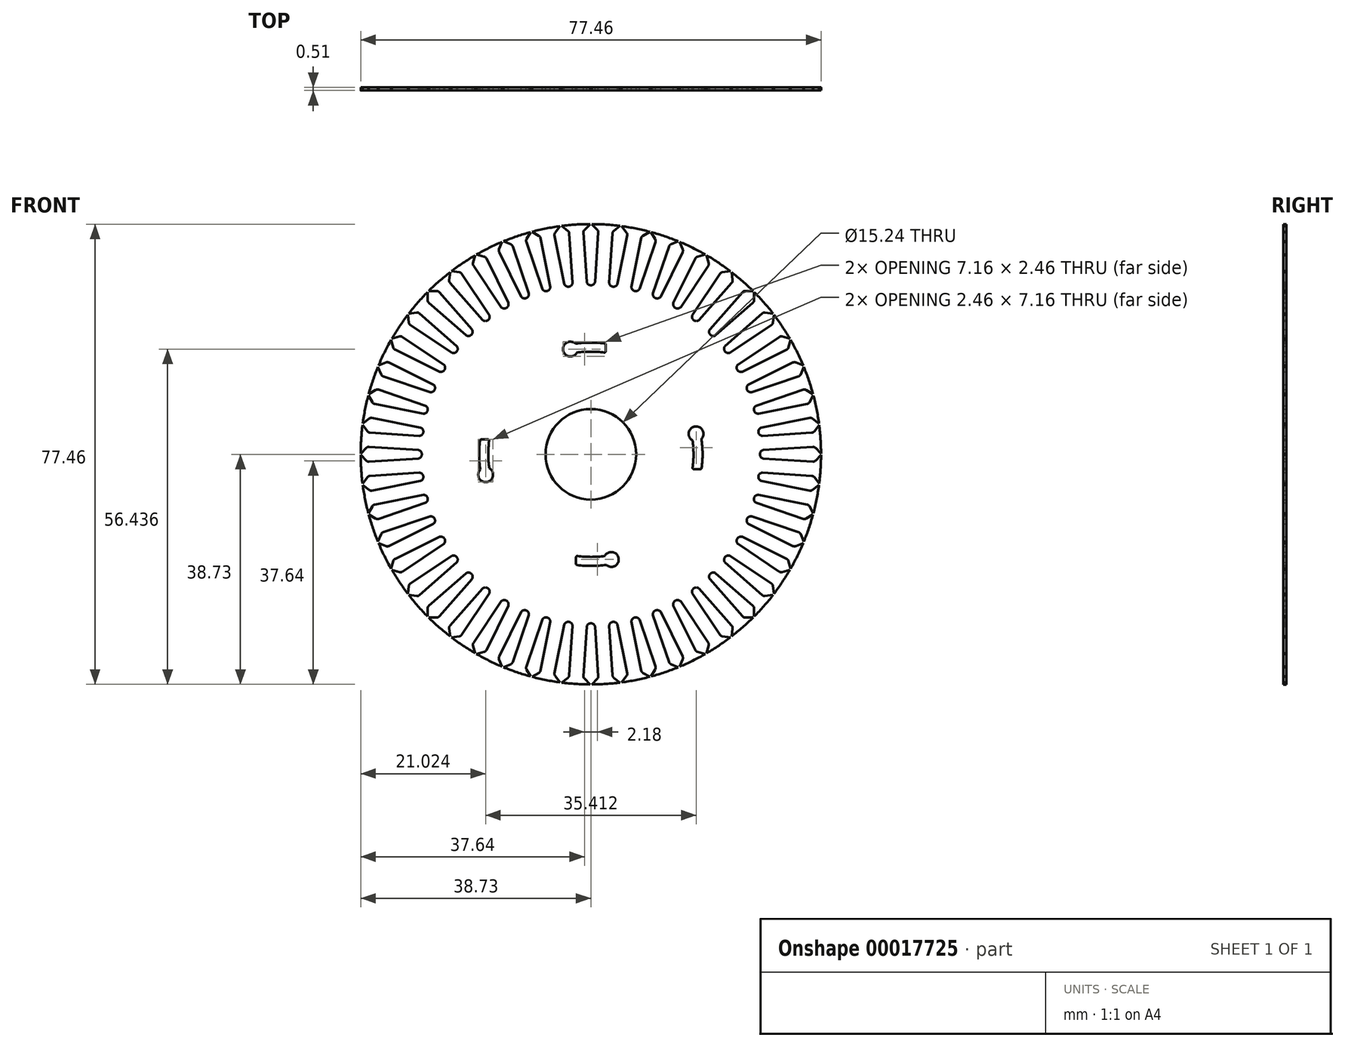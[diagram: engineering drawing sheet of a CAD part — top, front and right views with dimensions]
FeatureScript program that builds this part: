
annotation { "Feature Type Name" : "Feature", "Feature Type Description" : "" }
export const myFeature = defineFeature(function(context is Context, id is Id, definition is map)
    precondition{}
    {
        {
            var Q0;
            Q0=qCreatedBy(makeId("Front.planeOp"),FACE);
            var sketch = newSketch(context, id + "F0", { "sketchPlane" : qUnion([Q0])});
            skCircle(sketch, "E0", {"center": v(0, 0) * mm, "radius": 7.62 * mm});
            skArc(sketch, "E1", {"start": v(-0.12, 38.73) * mm, "mid": v(-2.53, 38.65) * mm, "end": v(-4.93, 38.42) * mm});
            skLineSegment(sketch, "E2", {"start": v(0, 0) * mm, "end": v(-4.84, 24.91) * mm, "construction": true});
            skArc(sketch, "E3", {"start": v(2.27, 17.12) * mm, "mid": v(-0.04, 17.27) * mm, "end": v(-2.35, 17.11) * mm});
            skArc(sketch, "E4", {"start": v(2.32, 18.65) * mm, "mid": v(-0.14, 18.8) * mm, "end": v(-2.6, 18.62) * mm});
            skArc(sketch, "E5", {"start": v(-2.6, 18.62) * mm, "mid": v(-4.67, 17.5) * mm, "end": v(-2.35, 17.11) * mm});
            skLineSegment(sketch, "E6", {"start": v(0, 17.1) * mm, "end": v(2.49, 17.1) * mm, "construction": true});
            skLineSegment(sketch, "E7", {"start": v(2.49, 17.32) * mm, "end": v(2.49, 18.46) * mm});
            skArc(sketch, "E8.1.0", {"start": v(-18.62, -2.6) * mm, "mid": v(-17.5, -4.67) * mm, "end": v(-17.11, -2.35) * mm});
            skArc(sketch, "E8.1.1", {"start": v(-18.65, 2.32) * mm, "mid": v(-18.8, -0.14) * mm, "end": v(-18.62, -2.6) * mm});
            skLineSegment(sketch, "E8.1.2", {"start": v(-17.32, 2.49) * mm, "end": v(-18.46, 2.49) * mm});
            skArc(sketch, "E8.1.3", {"start": v(-17.12, 2.27) * mm, "mid": v(-17.27, -0.04) * mm, "end": v(-17.11, -2.35) * mm});
            skArc(sketch, "E8.2.0", {"start": v(2.6, -18.62) * mm, "mid": v(4.67, -17.5) * mm, "end": v(2.35, -17.11) * mm});
            skArc(sketch, "E8.2.1", {"start": v(-2.32, -18.65) * mm, "mid": v(0.14, -18.8) * mm, "end": v(2.6, -18.62) * mm});
            skLineSegment(sketch, "E8.2.2", {"start": v(-2.49, -17.32) * mm, "end": v(-2.49, -18.46) * mm});
            skArc(sketch, "E8.2.3", {"start": v(-2.27, -17.12) * mm, "mid": v(0.04, -17.27) * mm, "end": v(2.35, -17.11) * mm});
            skArc(sketch, "E8.3.0", {"start": v(18.62, 2.6) * mm, "mid": v(17.5, 4.67) * mm, "end": v(17.11, 2.35) * mm});
            skArc(sketch, "E8.3.1", {"start": v(18.65, -2.32) * mm, "mid": v(18.8, 0.14) * mm, "end": v(18.62, 2.6) * mm});
            skLineSegment(sketch, "E8.3.2", {"start": v(17.32, -2.49) * mm, "end": v(18.46, -2.49) * mm});
            skArc(sketch, "E8.3.3", {"start": v(17.12, -2.27) * mm, "mid": v(17.27, 0.04) * mm, "end": v(17.11, 2.35) * mm});
            skPoint(sketch, "E9.visualSharp", {"position": v(2.49, 18.63) * mm});
            skArc(sketch, "E9.filletArc", {"start": v(2.49, 18.46) * mm, "mid": v(2.44, 18.59) * mm, "end": v(2.32, 18.65) * mm});
            skPoint(sketch, "E10.visualSharp", {"position": v(2.49, 17.1) * mm});
            skArc(sketch, "E10.filletArc", {"start": v(2.27, 17.12) * mm, "mid": v(2.42, 17.17) * mm, "end": v(2.49, 17.32) * mm});
            skPoint(sketch, "E11.visualSharp", {"position": v(-18.63, 2.49) * mm});
            skArc(sketch, "E11.filletArc", {"start": v(-18.46, 2.49) * mm, "mid": v(-18.59, 2.44) * mm, "end": v(-18.65, 2.32) * mm});
            skPoint(sketch, "E12.visualSharp", {"position": v(-17.1, 2.49) * mm});
            skArc(sketch, "E12.filletArc", {"start": v(-17.12, 2.27) * mm, "mid": v(-17.17, 2.42) * mm, "end": v(-17.32, 2.49) * mm});
            skPoint(sketch, "E13.visualSharp", {"position": v(-2.49, -18.63) * mm});
            skArc(sketch, "E13.filletArc", {"start": v(-2.49, -18.46) * mm, "mid": v(-2.44, -18.59) * mm, "end": v(-2.32, -18.65) * mm});
            skPoint(sketch, "E14.visualSharp", {"position": v(-2.49, -17.1) * mm});
            skArc(sketch, "E14.filletArc", {"start": v(-2.27, -17.12) * mm, "mid": v(-2.42, -17.17) * mm, "end": v(-2.49, -17.32) * mm});
            skPoint(sketch, "E15.visualSharp", {"position": v(18.63, -2.49) * mm});
            skArc(sketch, "E15.filletArc", {"start": v(18.46, -2.49) * mm, "mid": v(18.59, -2.44) * mm, "end": v(18.65, -2.32) * mm});
            skPoint(sketch, "E16.visualSharp", {"position": v(17.1, -2.49) * mm});
            skArc(sketch, "E16.filletArc", {"start": v(17.12, -2.27) * mm, "mid": v(17.17, -2.42) * mm, "end": v(17.32, -2.49) * mm});
            skLineSegment(sketch, "E17", {"start": v(0, 0) * mm, "end": v(5.53, 45) * mm, "construction": true});
            skLineSegment(sketch, "E18", {"start": v(-18.4, 38.5) * mm, "end": v(-0.35, 38.5) * mm, "construction": true});
            skPoint(sketch, "E19", {"position": v(-0.35, 38.5) * mm});
            skPoint(sketch, "E20", {"position": v(0.35, 38.5) * mm});
            skLineSegment(sketch, "E21", {"start": v(0.35, 38.5) * mm, "end": v(1.08, 37.77) * mm});
            skLineSegment(sketch, "E22", {"start": v(-0.35, 38.5) * mm, "end": v(-1.08, 37.77) * mm});
            skLineSegment(sketch, "E23", {"start": v(-0.35, 38.5) * mm, "end": v(-0.12, 38.73) * mm});
            skLineSegment(sketch, "E24", {"start": v(0.35, 38.5) * mm, "end": v(0.12, 38.73) * mm});
            skLineSegment(sketch, "E25", {"start": v(0.7, 29) * mm, "end": v(1.25, 37.34) * mm});
            skLineSegment(sketch, "E26", {"start": v(-0.7, 29) * mm, "end": v(-1.25, 37.34) * mm});
            skPoint(sketch, "E27", {"position": v(-1.32, 38.5) * mm});
            skPoint(sketch, "E28", {"position": v(1.32, 38.5) * mm});
            skPoint(sketch, "E29.newPointA", {"position": v(-1.7, 44.35) * mm});
            skArc(sketch, "E29.filletArc", {"start": v(-1.08, 37.77) * mm, "mid": v(-1.21, 37.58) * mm, "end": v(-1.25, 37.34) * mm});
            skPoint(sketch, "E30.newPointB", {"position": v(1.7, 44.35) * mm});
            skArc(sketch, "E30.filletArc", {"start": v(1.25, 37.34) * mm, "mid": v(1.21, 37.58) * mm, "end": v(1.08, 37.77) * mm});
            skLineSegment(sketch, "E31.trimOffspring", {"start": v(0.35, 38.5) * mm, "end": v(19.4, 38.5) * mm, "construction": true});
            skPoint(sketch, "E32.orphan", {"position": v(-0.67, 28.44) * mm});
            skArc(sketch, "E33.trimOffspring", {"start": v(-0.67, 28.44) * mm, "mid": v(0, -28.45) * mm, "end": v(0.67, 28.44) * mm, "construction": true});
            skArc(sketch, "E34.trimOffspring", {"start": v(-0.7, 29) * mm, "mid": v(0, 28.44) * mm, "end": v(0.7, 29) * mm});
            skLineSegment(sketch, "E35.1.0", {"start": v(-5.37, 38.13) * mm, "end": v(-5.18, 38.39) * mm});
            skLineSegment(sketch, "E35.1.1", {"start": v(-5.37, 38.13) * mm, "end": v(-6, 37.3) * mm});
            skArc(sketch, "E35.1.2", {"start": v(-6, 37.3) * mm, "mid": v(-6.1, 37.1) * mm, "end": v(-6.1, 36.86) * mm});
            skLineSegment(sketch, "E35.1.3", {"start": v(-4.48, 28.66) * mm, "end": v(-6.1, 36.86) * mm});
            skArc(sketch, "E35.1.4", {"start": v(-4.48, 28.66) * mm, "mid": v(-3.71, 28.2) * mm, "end": v(-3.09, 28.84) * mm});
            skLineSegment(sketch, "E35.1.5", {"start": v(-3.09, 28.84) * mm, "end": v(-3.64, 37.19) * mm});
            skArc(sketch, "E35.1.6", {"start": v(-3.64, 37.19) * mm, "mid": v(-3.7, 37.41) * mm, "end": v(-3.86, 37.6) * mm});
            skLineSegment(sketch, "E35.1.7", {"start": v(-4.68, 38.22) * mm, "end": v(-3.86, 37.6) * mm});
            skLineSegment(sketch, "E35.1.8", {"start": v(-4.68, 38.22) * mm, "end": v(-4.93, 38.42) * mm});
            skLineSegment(sketch, "E35.2.0", {"start": v(-10.3, 37.1) * mm, "end": v(-10.14, 37.38) * mm});
            skLineSegment(sketch, "E35.2.1", {"start": v(-10.3, 37.1) * mm, "end": v(-10.82, 36.2) * mm});
            skArc(sketch, "E35.2.2", {"start": v(-10.82, 36.2) * mm, "mid": v(-10.9, 35.98) * mm, "end": v(-10.87, 35.75) * mm});
            skLineSegment(sketch, "E35.2.3", {"start": v(-8.18, 27.83) * mm, "end": v(-10.87, 35.75) * mm});
            skArc(sketch, "E35.2.4", {"start": v(-8.18, 27.83) * mm, "mid": v(-7.36, 27.47) * mm, "end": v(-6.83, 28.2) * mm});
            skLineSegment(sketch, "E35.2.5", {"start": v(-6.83, 28.2) * mm, "end": v(-8.46, 36.4) * mm});
            skArc(sketch, "E35.2.6", {"start": v(-8.46, 36.4) * mm, "mid": v(-8.56, 36.6) * mm, "end": v(-8.73, 36.77) * mm});
            skLineSegment(sketch, "E35.2.7", {"start": v(-9.63, 37.29) * mm, "end": v(-8.73, 36.77) * mm});
            skLineSegment(sketch, "E35.2.8", {"start": v(-9.63, 37.29) * mm, "end": v(-9.9, 37.45) * mm});
            skLineSegment(sketch, "E35.3.0", {"start": v(-15.06, 35.44) * mm, "end": v(-14.94, 35.74) * mm});
            skLineSegment(sketch, "E35.3.1", {"start": v(-15.06, 35.44) * mm, "end": v(-15.46, 34.48) * mm});
            skArc(sketch, "E35.3.2", {"start": v(-15.46, 34.48) * mm, "mid": v(-15.5, 34.25) * mm, "end": v(-15.44, 34.02) * mm});
            skLineSegment(sketch, "E35.3.3", {"start": v(-11.75, 26.52) * mm, "end": v(-15.44, 34.02) * mm});
            skArc(sketch, "E35.3.4", {"start": v(-11.75, 26.52) * mm, "mid": v(-10.88, 26.28) * mm, "end": v(-10.45, 27.06) * mm});
            skLineSegment(sketch, "E35.3.5", {"start": v(-10.45, 27.06) * mm, "end": v(-13.14, 34.98) * mm});
            skArc(sketch, "E35.3.6", {"start": v(-13.14, 34.98) * mm, "mid": v(-13.26, 35.18) * mm, "end": v(-13.46, 35.31) * mm});
            skLineSegment(sketch, "E35.3.7", {"start": v(-14.41, 35.7) * mm, "end": v(-13.46, 35.31) * mm});
            skLineSegment(sketch, "E35.3.8", {"start": v(-14.41, 35.7) * mm, "end": v(-14.71, 35.83) * mm});
            skLineSegment(sketch, "E35.4.0", {"start": v(-19.56, 33.17) * mm, "end": v(-19.47, 33.48) * mm});
            skLineSegment(sketch, "E35.4.1", {"start": v(-19.56, 33.17) * mm, "end": v(-19.82, 32.17) * mm});
            skArc(sketch, "E35.4.2", {"start": v(-19.82, 32.17) * mm, "mid": v(-19.84, 31.94) * mm, "end": v(-19.75, 31.72) * mm});
            skLineSegment(sketch, "E35.4.3", {"start": v(-15.1, 24.76) * mm, "end": v(-19.75, 31.72) * mm});
            skArc(sketch, "E35.4.4", {"start": v(-15.1, 24.76) * mm, "mid": v(-14.22, 24.63) * mm, "end": v(-13.9, 25.46) * mm});
            skLineSegment(sketch, "E35.4.5", {"start": v(-13.9, 25.46) * mm, "end": v(-17.6, 32.96) * mm});
            skArc(sketch, "E35.4.6", {"start": v(-17.6, 32.96) * mm, "mid": v(-17.74, 33.15) * mm, "end": v(-17.95, 33.25) * mm});
            skLineSegment(sketch, "E35.4.7", {"start": v(-18.95, 33.52) * mm, "end": v(-17.95, 33.25) * mm});
            skLineSegment(sketch, "E35.4.8", {"start": v(-18.95, 33.52) * mm, "end": v(-19.26, 33.6) * mm});
            skLineSegment(sketch, "E35.5.0", {"start": v(-23.72, 30.34) * mm, "end": v(-23.68, 30.66) * mm});
            skLineSegment(sketch, "E35.5.1", {"start": v(-23.72, 30.34) * mm, "end": v(-23.85, 29.3) * mm});
            skArc(sketch, "E35.5.2", {"start": v(-23.85, 29.3) * mm, "mid": v(-23.84, 29.07) * mm, "end": v(-23.72, 28.87) * mm});
            skLineSegment(sketch, "E35.5.3", {"start": v(-18.21, 22.58) * mm, "end": v(-23.72, 28.87) * mm});
            skArc(sketch, "E35.5.4", {"start": v(-18.21, 22.58) * mm, "mid": v(-17.31, 22.56) * mm, "end": v(-17.1, 23.43) * mm});
            skLineSegment(sketch, "E35.5.5", {"start": v(-17.1, 23.43) * mm, "end": v(-21.75, 30.38) * mm});
            skArc(sketch, "E35.5.6", {"start": v(-21.75, 30.38) * mm, "mid": v(-21.91, 30.55) * mm, "end": v(-22.14, 30.63) * mm});
            skLineSegment(sketch, "E35.5.7", {"start": v(-23.16, 30.76) * mm, "end": v(-22.14, 30.63) * mm});
            skLineSegment(sketch, "E35.5.8", {"start": v(-23.16, 30.76) * mm, "end": v(-23.48, 30.8) * mm});
            skLineSegment(sketch, "E35.6.0", {"start": v(-27.48, 26.98) * mm, "end": v(-27.48, 27.3) * mm});
            skLineSegment(sketch, "E35.6.1", {"start": v(-27.48, 26.98) * mm, "end": v(-27.48, 25.95) * mm});
            skArc(sketch, "E35.6.2", {"start": v(-27.48, 25.95) * mm, "mid": v(-27.43, 25.71) * mm, "end": v(-27.29, 25.53) * mm});
            skLineSegment(sketch, "E35.6.3", {"start": v(-21, 20) * mm, "end": v(-27.29, 25.53) * mm});
            skArc(sketch, "E35.6.4", {"start": v(-21, 20) * mm, "mid": v(-20.11, 20.11) * mm, "end": v(-20, 21) * mm});
            skLineSegment(sketch, "E35.6.5", {"start": v(-20, 21) * mm, "end": v(-25.53, 27.29) * mm});
            skArc(sketch, "E35.6.6", {"start": v(-25.53, 27.29) * mm, "mid": v(-25.71, 27.43) * mm, "end": v(-25.95, 27.48) * mm});
            skLineSegment(sketch, "E35.6.7", {"start": v(-26.98, 27.48) * mm, "end": v(-25.95, 27.48) * mm});
            skLineSegment(sketch, "E35.6.8", {"start": v(-26.98, 27.48) * mm, "end": v(-27.3, 27.48) * mm});
            skLineSegment(sketch, "E35.7.0", {"start": v(-30.76, 23.16) * mm, "end": v(-30.8, 23.48) * mm});
            skLineSegment(sketch, "E35.7.1", {"start": v(-30.76, 23.16) * mm, "end": v(-30.63, 22.14) * mm});
            skArc(sketch, "E35.7.2", {"start": v(-30.63, 22.14) * mm, "mid": v(-30.55, 21.91) * mm, "end": v(-30.38, 21.75) * mm});
            skLineSegment(sketch, "E35.7.3", {"start": v(-23.43, 17.1) * mm, "end": v(-30.38, 21.75) * mm});
            skArc(sketch, "E35.7.4", {"start": v(-23.43, 17.1) * mm, "mid": v(-22.56, 17.31) * mm, "end": v(-22.58, 18.21) * mm});
            skLineSegment(sketch, "E35.7.5", {"start": v(-22.58, 18.21) * mm, "end": v(-28.87, 23.72) * mm});
            skArc(sketch, "E35.7.6", {"start": v(-28.87, 23.72) * mm, "mid": v(-29.07, 23.84) * mm, "end": v(-29.3, 23.85) * mm});
            skLineSegment(sketch, "E35.7.7", {"start": v(-30.34, 23.72) * mm, "end": v(-29.3, 23.85) * mm});
            skLineSegment(sketch, "E35.7.8", {"start": v(-30.34, 23.72) * mm, "end": v(-30.66, 23.68) * mm});
            skLineSegment(sketch, "E35.8.0", {"start": v(-33.52, 18.95) * mm, "end": v(-33.6, 19.26) * mm});
            skLineSegment(sketch, "E35.8.1", {"start": v(-33.52, 18.95) * mm, "end": v(-33.25, 17.95) * mm});
            skArc(sketch, "E35.8.2", {"start": v(-33.25, 17.95) * mm, "mid": v(-33.15, 17.74) * mm, "end": v(-32.96, 17.6) * mm});
            skLineSegment(sketch, "E35.8.3", {"start": v(-25.46, 13.9) * mm, "end": v(-32.96, 17.6) * mm});
            skArc(sketch, "E35.8.4", {"start": v(-25.46, 13.9) * mm, "mid": v(-24.63, 14.22) * mm, "end": v(-24.76, 15.1) * mm});
            skLineSegment(sketch, "E35.8.5", {"start": v(-24.76, 15.1) * mm, "end": v(-31.72, 19.75) * mm});
            skArc(sketch, "E35.8.6", {"start": v(-31.72, 19.75) * mm, "mid": v(-31.94, 19.84) * mm, "end": v(-32.17, 19.82) * mm});
            skLineSegment(sketch, "E35.8.7", {"start": v(-33.17, 19.56) * mm, "end": v(-32.17, 19.82) * mm});
            skLineSegment(sketch, "E35.8.8", {"start": v(-33.17, 19.56) * mm, "end": v(-33.48, 19.47) * mm});
            skLineSegment(sketch, "E35.9.0", {"start": v(-35.7, 14.41) * mm, "end": v(-35.83, 14.71) * mm});
            skLineSegment(sketch, "E35.9.1", {"start": v(-35.7, 14.41) * mm, "end": v(-35.31, 13.46) * mm});
            skArc(sketch, "E35.9.2", {"start": v(-35.31, 13.46) * mm, "mid": v(-35.18, 13.26) * mm, "end": v(-34.98, 13.14) * mm});
            skLineSegment(sketch, "E35.9.3", {"start": v(-27.06, 10.45) * mm, "end": v(-34.98, 13.14) * mm});
            skArc(sketch, "E35.9.4", {"start": v(-27.06, 10.45) * mm, "mid": v(-26.28, 10.88) * mm, "end": v(-26.52, 11.75) * mm});
            skLineSegment(sketch, "E35.9.5", {"start": v(-26.52, 11.75) * mm, "end": v(-34.02, 15.44) * mm});
            skArc(sketch, "E35.9.6", {"start": v(-34.02, 15.44) * mm, "mid": v(-34.25, 15.5) * mm, "end": v(-34.48, 15.46) * mm});
            skLineSegment(sketch, "E35.9.7", {"start": v(-35.44, 15.06) * mm, "end": v(-34.48, 15.46) * mm});
            skLineSegment(sketch, "E35.9.8", {"start": v(-35.44, 15.06) * mm, "end": v(-35.74, 14.94) * mm});
            skLineSegment(sketch, "E35.10.0", {"start": v(-37.29, 9.63) * mm, "end": v(-37.45, 9.9) * mm});
            skLineSegment(sketch, "E35.10.1", {"start": v(-37.29, 9.63) * mm, "end": v(-36.77, 8.73) * mm});
            skArc(sketch, "E35.10.2", {"start": v(-36.77, 8.73) * mm, "mid": v(-36.6, 8.56) * mm, "end": v(-36.4, 8.46) * mm});
            skLineSegment(sketch, "E35.10.3", {"start": v(-28.2, 6.83) * mm, "end": v(-36.4, 8.46) * mm});
            skArc(sketch, "E35.10.4", {"start": v(-28.2, 6.83) * mm, "mid": v(-27.47, 7.36) * mm, "end": v(-27.83, 8.18) * mm});
            skLineSegment(sketch, "E35.10.5", {"start": v(-27.83, 8.18) * mm, "end": v(-35.75, 10.87) * mm});
            skArc(sketch, "E35.10.6", {"start": v(-35.75, 10.87) * mm, "mid": v(-35.98, 10.9) * mm, "end": v(-36.2, 10.82) * mm});
            skLineSegment(sketch, "E35.10.7", {"start": v(-37.1, 10.3) * mm, "end": v(-36.2, 10.82) * mm});
            skLineSegment(sketch, "E35.10.8", {"start": v(-37.1, 10.3) * mm, "end": v(-37.38, 10.14) * mm});
            skLineSegment(sketch, "E35.11.0", {"start": v(-38.22, 4.68) * mm, "end": v(-38.42, 4.93) * mm});
            skLineSegment(sketch, "E35.11.1", {"start": v(-38.22, 4.68) * mm, "end": v(-37.6, 3.86) * mm});
            skArc(sketch, "E35.11.2", {"start": v(-37.6, 3.86) * mm, "mid": v(-37.41, 3.7) * mm, "end": v(-37.19, 3.64) * mm});
            skLineSegment(sketch, "E35.11.3", {"start": v(-28.84, 3.09) * mm, "end": v(-37.19, 3.64) * mm});
            skArc(sketch, "E35.11.4", {"start": v(-28.84, 3.09) * mm, "mid": v(-28.2, 3.71) * mm, "end": v(-28.66, 4.48) * mm});
            skLineSegment(sketch, "E35.11.5", {"start": v(-28.66, 4.48) * mm, "end": v(-36.86, 6.1) * mm});
            skArc(sketch, "E35.11.6", {"start": v(-36.86, 6.1) * mm, "mid": v(-37.1, 6.1) * mm, "end": v(-37.3, 6) * mm});
            skLineSegment(sketch, "E35.11.7", {"start": v(-38.13, 5.37) * mm, "end": v(-37.3, 6) * mm});
            skLineSegment(sketch, "E35.11.8", {"start": v(-38.13, 5.37) * mm, "end": v(-38.39, 5.18) * mm});
            skLineSegment(sketch, "E35.12.0", {"start": v(-38.5, -0.35) * mm, "end": v(-38.73, -0.12) * mm});
            skLineSegment(sketch, "E35.12.1", {"start": v(-38.5, -0.35) * mm, "end": v(-37.77, -1.08) * mm});
            skArc(sketch, "E35.12.2", {"start": v(-37.77, -1.08) * mm, "mid": v(-37.58, -1.21) * mm, "end": v(-37.34, -1.25) * mm});
            skLineSegment(sketch, "E35.12.3", {"start": v(-29, -0.7) * mm, "end": v(-37.34, -1.25) * mm});
            skArc(sketch, "E35.12.4", {"start": v(-29, -0.7) * mm, "mid": v(-28.44, 0) * mm, "end": v(-29, 0.7) * mm});
            skLineSegment(sketch, "E35.12.5", {"start": v(-29, 0.7) * mm, "end": v(-37.34, 1.25) * mm});
            skArc(sketch, "E35.12.6", {"start": v(-37.34, 1.25) * mm, "mid": v(-37.58, 1.21) * mm, "end": v(-37.77, 1.08) * mm});
            skLineSegment(sketch, "E35.12.7", {"start": v(-38.5, 0.35) * mm, "end": v(-37.77, 1.08) * mm});
            skLineSegment(sketch, "E35.12.8", {"start": v(-38.5, 0.35) * mm, "end": v(-38.73, 0.12) * mm});
            skLineSegment(sketch, "E35.13.0", {"start": v(-38.13, -5.37) * mm, "end": v(-38.39, -5.18) * mm});
            skLineSegment(sketch, "E35.13.1", {"start": v(-38.13, -5.37) * mm, "end": v(-37.3, -6) * mm});
            skArc(sketch, "E35.13.2", {"start": v(-37.3, -6) * mm, "mid": v(-37.1, -6.1) * mm, "end": v(-36.86, -6.1) * mm});
            skLineSegment(sketch, "E35.13.3", {"start": v(-28.66, -4.48) * mm, "end": v(-36.86, -6.1) * mm});
            skArc(sketch, "E35.13.4", {"start": v(-28.66, -4.48) * mm, "mid": v(-28.2, -3.71) * mm, "end": v(-28.84, -3.09) * mm});
            skLineSegment(sketch, "E35.13.5", {"start": v(-28.84, -3.09) * mm, "end": v(-37.19, -3.64) * mm});
            skArc(sketch, "E35.13.6", {"start": v(-37.19, -3.64) * mm, "mid": v(-37.41, -3.7) * mm, "end": v(-37.6, -3.86) * mm});
            skLineSegment(sketch, "E35.13.7", {"start": v(-38.22, -4.68) * mm, "end": v(-37.6, -3.86) * mm});
            skLineSegment(sketch, "E35.13.8", {"start": v(-38.22, -4.68) * mm, "end": v(-38.42, -4.93) * mm});
            skLineSegment(sketch, "E35.14.0", {"start": v(-37.1, -10.3) * mm, "end": v(-37.38, -10.14) * mm});
            skLineSegment(sketch, "E35.14.1", {"start": v(-37.1, -10.3) * mm, "end": v(-36.2, -10.82) * mm});
            skArc(sketch, "E35.14.2", {"start": v(-36.2, -10.82) * mm, "mid": v(-35.98, -10.9) * mm, "end": v(-35.75, -10.87) * mm});
            skLineSegment(sketch, "E35.14.3", {"start": v(-27.83, -8.18) * mm, "end": v(-35.75, -10.87) * mm});
            skArc(sketch, "E35.14.4", {"start": v(-27.83, -8.18) * mm, "mid": v(-27.47, -7.36) * mm, "end": v(-28.2, -6.83) * mm});
            skLineSegment(sketch, "E35.14.5", {"start": v(-28.2, -6.83) * mm, "end": v(-36.4, -8.46) * mm});
            skArc(sketch, "E35.14.6", {"start": v(-36.4, -8.46) * mm, "mid": v(-36.6, -8.56) * mm, "end": v(-36.77, -8.73) * mm});
            skLineSegment(sketch, "E35.14.7", {"start": v(-37.29, -9.63) * mm, "end": v(-36.77, -8.73) * mm});
            skLineSegment(sketch, "E35.14.8", {"start": v(-37.29, -9.63) * mm, "end": v(-37.45, -9.9) * mm});
            skLineSegment(sketch, "E35.15.0", {"start": v(-35.44, -15.06) * mm, "end": v(-35.74, -14.94) * mm});
            skLineSegment(sketch, "E35.15.1", {"start": v(-35.44, -15.06) * mm, "end": v(-34.48, -15.46) * mm});
            skArc(sketch, "E35.15.2", {"start": v(-34.48, -15.46) * mm, "mid": v(-34.25, -15.5) * mm, "end": v(-34.02, -15.44) * mm});
            skLineSegment(sketch, "E35.15.3", {"start": v(-26.52, -11.75) * mm, "end": v(-34.02, -15.44) * mm});
            skArc(sketch, "E35.15.4", {"start": v(-26.52, -11.75) * mm, "mid": v(-26.28, -10.88) * mm, "end": v(-27.06, -10.45) * mm});
            skLineSegment(sketch, "E35.15.5", {"start": v(-27.06, -10.45) * mm, "end": v(-34.98, -13.14) * mm});
            skArc(sketch, "E35.15.6", {"start": v(-34.98, -13.14) * mm, "mid": v(-35.18, -13.26) * mm, "end": v(-35.31, -13.46) * mm});
            skLineSegment(sketch, "E35.15.7", {"start": v(-35.7, -14.41) * mm, "end": v(-35.31, -13.46) * mm});
            skLineSegment(sketch, "E35.15.8", {"start": v(-35.7, -14.41) * mm, "end": v(-35.83, -14.71) * mm});
            skLineSegment(sketch, "E35.16.0", {"start": v(-33.17, -19.56) * mm, "end": v(-33.48, -19.47) * mm});
            skLineSegment(sketch, "E35.16.1", {"start": v(-33.17, -19.56) * mm, "end": v(-32.17, -19.82) * mm});
            skArc(sketch, "E35.16.2", {"start": v(-32.17, -19.82) * mm, "mid": v(-31.94, -19.84) * mm, "end": v(-31.72, -19.75) * mm});
            skLineSegment(sketch, "E35.16.3", {"start": v(-24.76, -15.1) * mm, "end": v(-31.72, -19.75) * mm});
            skArc(sketch, "E35.16.4", {"start": v(-24.76, -15.1) * mm, "mid": v(-24.63, -14.22) * mm, "end": v(-25.46, -13.9) * mm});
            skLineSegment(sketch, "E35.16.5", {"start": v(-25.46, -13.9) * mm, "end": v(-32.96, -17.6) * mm});
            skArc(sketch, "E35.16.6", {"start": v(-32.96, -17.6) * mm, "mid": v(-33.15, -17.74) * mm, "end": v(-33.25, -17.95) * mm});
            skLineSegment(sketch, "E35.16.7", {"start": v(-33.52, -18.95) * mm, "end": v(-33.25, -17.95) * mm});
            skLineSegment(sketch, "E35.16.8", {"start": v(-33.52, -18.95) * mm, "end": v(-33.6, -19.26) * mm});
            skLineSegment(sketch, "E35.17.0", {"start": v(-30.34, -23.72) * mm, "end": v(-30.66, -23.68) * mm});
            skLineSegment(sketch, "E35.17.1", {"start": v(-30.34, -23.72) * mm, "end": v(-29.3, -23.85) * mm});
            skArc(sketch, "E35.17.2", {"start": v(-29.3, -23.85) * mm, "mid": v(-29.07, -23.84) * mm, "end": v(-28.87, -23.72) * mm});
            skLineSegment(sketch, "E35.17.3", {"start": v(-22.58, -18.21) * mm, "end": v(-28.87, -23.72) * mm});
            skArc(sketch, "E35.17.4", {"start": v(-22.58, -18.21) * mm, "mid": v(-22.56, -17.31) * mm, "end": v(-23.43, -17.1) * mm});
            skLineSegment(sketch, "E35.17.5", {"start": v(-23.43, -17.1) * mm, "end": v(-30.38, -21.75) * mm});
            skArc(sketch, "E35.17.6", {"start": v(-30.38, -21.75) * mm, "mid": v(-30.55, -21.91) * mm, "end": v(-30.63, -22.14) * mm});
            skLineSegment(sketch, "E35.17.7", {"start": v(-30.76, -23.16) * mm, "end": v(-30.63, -22.14) * mm});
            skLineSegment(sketch, "E35.17.8", {"start": v(-30.76, -23.16) * mm, "end": v(-30.8, -23.48) * mm});
            skLineSegment(sketch, "E35.18.0", {"start": v(-26.98, -27.48) * mm, "end": v(-27.3, -27.48) * mm});
            skLineSegment(sketch, "E35.18.1", {"start": v(-26.98, -27.48) * mm, "end": v(-25.95, -27.48) * mm});
            skArc(sketch, "E35.18.2", {"start": v(-25.95, -27.48) * mm, "mid": v(-25.71, -27.43) * mm, "end": v(-25.53, -27.29) * mm});
            skLineSegment(sketch, "E35.18.3", {"start": v(-20, -21) * mm, "end": v(-25.53, -27.29) * mm});
            skArc(sketch, "E35.18.4", {"start": v(-20, -21) * mm, "mid": v(-20.11, -20.11) * mm, "end": v(-21, -20) * mm});
            skLineSegment(sketch, "E35.18.5", {"start": v(-21, -20) * mm, "end": v(-27.29, -25.53) * mm});
            skArc(sketch, "E35.18.6", {"start": v(-27.29, -25.53) * mm, "mid": v(-27.43, -25.71) * mm, "end": v(-27.48, -25.95) * mm});
            skLineSegment(sketch, "E35.18.7", {"start": v(-27.48, -26.98) * mm, "end": v(-27.48, -25.95) * mm});
            skLineSegment(sketch, "E35.18.8", {"start": v(-27.48, -26.98) * mm, "end": v(-27.48, -27.3) * mm});
            skLineSegment(sketch, "E35.19.0", {"start": v(-23.16, -30.76) * mm, "end": v(-23.48, -30.8) * mm});
            skLineSegment(sketch, "E35.19.1", {"start": v(-23.16, -30.76) * mm, "end": v(-22.14, -30.63) * mm});
            skArc(sketch, "E35.19.2", {"start": v(-22.14, -30.63) * mm, "mid": v(-21.91, -30.55) * mm, "end": v(-21.75, -30.38) * mm});
            skLineSegment(sketch, "E35.19.3", {"start": v(-17.1, -23.43) * mm, "end": v(-21.75, -30.38) * mm});
            skArc(sketch, "E35.19.4", {"start": v(-17.1, -23.43) * mm, "mid": v(-17.31, -22.56) * mm, "end": v(-18.21, -22.58) * mm});
            skLineSegment(sketch, "E35.19.5", {"start": v(-18.21, -22.58) * mm, "end": v(-23.72, -28.87) * mm});
            skArc(sketch, "E35.19.6", {"start": v(-23.72, -28.87) * mm, "mid": v(-23.84, -29.07) * mm, "end": v(-23.85, -29.3) * mm});
            skLineSegment(sketch, "E35.19.7", {"start": v(-23.72, -30.34) * mm, "end": v(-23.85, -29.3) * mm});
            skLineSegment(sketch, "E35.19.8", {"start": v(-23.72, -30.34) * mm, "end": v(-23.68, -30.66) * mm});
            skLineSegment(sketch, "E35.20.0", {"start": v(-18.95, -33.52) * mm, "end": v(-19.26, -33.6) * mm});
            skLineSegment(sketch, "E35.20.1", {"start": v(-18.95, -33.52) * mm, "end": v(-17.95, -33.25) * mm});
            skArc(sketch, "E35.20.2", {"start": v(-17.95, -33.25) * mm, "mid": v(-17.74, -33.15) * mm, "end": v(-17.6, -32.96) * mm});
            skLineSegment(sketch, "E35.20.3", {"start": v(-13.9, -25.46) * mm, "end": v(-17.6, -32.96) * mm});
            skArc(sketch, "E35.20.4", {"start": v(-13.9, -25.46) * mm, "mid": v(-14.22, -24.63) * mm, "end": v(-15.1, -24.76) * mm});
            skLineSegment(sketch, "E35.20.5", {"start": v(-15.1, -24.76) * mm, "end": v(-19.75, -31.72) * mm});
            skArc(sketch, "E35.20.6", {"start": v(-19.75, -31.72) * mm, "mid": v(-19.84, -31.94) * mm, "end": v(-19.82, -32.17) * mm});
            skLineSegment(sketch, "E35.20.7", {"start": v(-19.56, -33.17) * mm, "end": v(-19.82, -32.17) * mm});
            skLineSegment(sketch, "E35.20.8", {"start": v(-19.56, -33.17) * mm, "end": v(-19.47, -33.48) * mm});
            skLineSegment(sketch, "E35.21.0", {"start": v(-14.41, -35.7) * mm, "end": v(-14.71, -35.83) * mm});
            skLineSegment(sketch, "E35.21.1", {"start": v(-14.41, -35.7) * mm, "end": v(-13.46, -35.31) * mm});
            skArc(sketch, "E35.21.2", {"start": v(-13.46, -35.31) * mm, "mid": v(-13.26, -35.18) * mm, "end": v(-13.14, -34.98) * mm});
            skLineSegment(sketch, "E35.21.3", {"start": v(-10.45, -27.06) * mm, "end": v(-13.14, -34.98) * mm});
            skArc(sketch, "E35.21.4", {"start": v(-10.45, -27.06) * mm, "mid": v(-10.88, -26.28) * mm, "end": v(-11.75, -26.52) * mm});
            skLineSegment(sketch, "E35.21.5", {"start": v(-11.75, -26.52) * mm, "end": v(-15.44, -34.02) * mm});
            skArc(sketch, "E35.21.6", {"start": v(-15.44, -34.02) * mm, "mid": v(-15.5, -34.25) * mm, "end": v(-15.46, -34.48) * mm});
            skLineSegment(sketch, "E35.21.7", {"start": v(-15.06, -35.44) * mm, "end": v(-15.46, -34.48) * mm});
            skLineSegment(sketch, "E35.21.8", {"start": v(-15.06, -35.44) * mm, "end": v(-14.94, -35.74) * mm});
            skLineSegment(sketch, "E35.22.0", {"start": v(-9.63, -37.29) * mm, "end": v(-9.9, -37.45) * mm});
            skLineSegment(sketch, "E35.22.1", {"start": v(-9.63, -37.29) * mm, "end": v(-8.73, -36.77) * mm});
            skArc(sketch, "E35.22.2", {"start": v(-8.73, -36.77) * mm, "mid": v(-8.56, -36.6) * mm, "end": v(-8.46, -36.4) * mm});
            skLineSegment(sketch, "E35.22.3", {"start": v(-6.83, -28.2) * mm, "end": v(-8.46, -36.4) * mm});
            skArc(sketch, "E35.22.4", {"start": v(-6.83, -28.2) * mm, "mid": v(-7.36, -27.47) * mm, "end": v(-8.18, -27.83) * mm});
            skLineSegment(sketch, "E35.22.5", {"start": v(-8.18, -27.83) * mm, "end": v(-10.87, -35.75) * mm});
            skArc(sketch, "E35.22.6", {"start": v(-10.87, -35.75) * mm, "mid": v(-10.9, -35.98) * mm, "end": v(-10.82, -36.2) * mm});
            skLineSegment(sketch, "E35.22.7", {"start": v(-10.3, -37.1) * mm, "end": v(-10.82, -36.2) * mm});
            skLineSegment(sketch, "E35.22.8", {"start": v(-10.3, -37.1) * mm, "end": v(-10.14, -37.38) * mm});
            skLineSegment(sketch, "E35.23.0", {"start": v(-4.68, -38.22) * mm, "end": v(-4.93, -38.42) * mm});
            skLineSegment(sketch, "E35.23.1", {"start": v(-4.68, -38.22) * mm, "end": v(-3.86, -37.6) * mm});
            skArc(sketch, "E35.23.2", {"start": v(-3.86, -37.6) * mm, "mid": v(-3.7, -37.41) * mm, "end": v(-3.64, -37.19) * mm});
            skLineSegment(sketch, "E35.23.3", {"start": v(-3.09, -28.84) * mm, "end": v(-3.64, -37.19) * mm});
            skArc(sketch, "E35.23.4", {"start": v(-3.09, -28.84) * mm, "mid": v(-3.71, -28.2) * mm, "end": v(-4.48, -28.66) * mm});
            skLineSegment(sketch, "E35.23.5", {"start": v(-4.48, -28.66) * mm, "end": v(-6.1, -36.86) * mm});
            skArc(sketch, "E35.23.6", {"start": v(-6.1, -36.86) * mm, "mid": v(-6.1, -37.1) * mm, "end": v(-6, -37.3) * mm});
            skLineSegment(sketch, "E35.23.7", {"start": v(-5.37, -38.13) * mm, "end": v(-6, -37.3) * mm});
            skLineSegment(sketch, "E35.23.8", {"start": v(-5.37, -38.13) * mm, "end": v(-5.18, -38.39) * mm});
            skLineSegment(sketch, "E35.24.0", {"start": v(0.35, -38.5) * mm, "end": v(0.12, -38.73) * mm});
            skLineSegment(sketch, "E35.24.1", {"start": v(0.35, -38.5) * mm, "end": v(1.08, -37.77) * mm});
            skArc(sketch, "E35.24.2", {"start": v(1.08, -37.77) * mm, "mid": v(1.21, -37.58) * mm, "end": v(1.25, -37.34) * mm});
            skLineSegment(sketch, "E35.24.3", {"start": v(0.7, -29) * mm, "end": v(1.25, -37.34) * mm});
            skArc(sketch, "E35.24.4", {"start": v(0.7, -29) * mm, "mid": v(0, -28.44) * mm, "end": v(-0.7, -29) * mm});
            skLineSegment(sketch, "E35.24.5", {"start": v(-0.7, -29) * mm, "end": v(-1.25, -37.34) * mm});
            skArc(sketch, "E35.24.6", {"start": v(-1.25, -37.34) * mm, "mid": v(-1.21, -37.58) * mm, "end": v(-1.08, -37.77) * mm});
            skLineSegment(sketch, "E35.24.7", {"start": v(-0.35, -38.5) * mm, "end": v(-1.08, -37.77) * mm});
            skLineSegment(sketch, "E35.24.8", {"start": v(-0.35, -38.5) * mm, "end": v(-0.12, -38.73) * mm});
            skLineSegment(sketch, "E35.25.0", {"start": v(5.37, -38.13) * mm, "end": v(5.18, -38.39) * mm});
            skLineSegment(sketch, "E35.25.1", {"start": v(5.37, -38.13) * mm, "end": v(6, -37.3) * mm});
            skArc(sketch, "E35.25.2", {"start": v(6, -37.3) * mm, "mid": v(6.1, -37.1) * mm, "end": v(6.1, -36.86) * mm});
            skLineSegment(sketch, "E35.25.3", {"start": v(4.48, -28.66) * mm, "end": v(6.1, -36.86) * mm});
            skArc(sketch, "E35.25.4", {"start": v(4.48, -28.66) * mm, "mid": v(3.71, -28.2) * mm, "end": v(3.09, -28.84) * mm});
            skLineSegment(sketch, "E35.25.5", {"start": v(3.09, -28.84) * mm, "end": v(3.64, -37.19) * mm});
            skArc(sketch, "E35.25.6", {"start": v(3.64, -37.19) * mm, "mid": v(3.7, -37.41) * mm, "end": v(3.86, -37.6) * mm});
            skLineSegment(sketch, "E35.25.7", {"start": v(4.68, -38.22) * mm, "end": v(3.86, -37.6) * mm});
            skLineSegment(sketch, "E35.25.8", {"start": v(4.68, -38.22) * mm, "end": v(4.93, -38.42) * mm});
            skLineSegment(sketch, "E35.26.0", {"start": v(10.3, -37.1) * mm, "end": v(10.14, -37.38) * mm});
            skLineSegment(sketch, "E35.26.1", {"start": v(10.3, -37.1) * mm, "end": v(10.82, -36.2) * mm});
            skArc(sketch, "E35.26.2", {"start": v(10.82, -36.2) * mm, "mid": v(10.9, -35.98) * mm, "end": v(10.87, -35.75) * mm});
            skLineSegment(sketch, "E35.26.3", {"start": v(8.18, -27.83) * mm, "end": v(10.87, -35.75) * mm});
            skArc(sketch, "E35.26.4", {"start": v(8.18, -27.83) * mm, "mid": v(7.36, -27.47) * mm, "end": v(6.83, -28.2) * mm});
            skLineSegment(sketch, "E35.26.5", {"start": v(6.83, -28.2) * mm, "end": v(8.46, -36.4) * mm});
            skArc(sketch, "E35.26.6", {"start": v(8.46, -36.4) * mm, "mid": v(8.56, -36.6) * mm, "end": v(8.73, -36.77) * mm});
            skLineSegment(sketch, "E35.26.7", {"start": v(9.63, -37.29) * mm, "end": v(8.73, -36.77) * mm});
            skLineSegment(sketch, "E35.26.8", {"start": v(9.63, -37.29) * mm, "end": v(9.9, -37.45) * mm});
            skLineSegment(sketch, "E35.27.0", {"start": v(15.06, -35.44) * mm, "end": v(14.94, -35.74) * mm});
            skLineSegment(sketch, "E35.27.1", {"start": v(15.06, -35.44) * mm, "end": v(15.46, -34.48) * mm});
            skArc(sketch, "E35.27.2", {"start": v(15.46, -34.48) * mm, "mid": v(15.5, -34.25) * mm, "end": v(15.44, -34.02) * mm});
            skLineSegment(sketch, "E35.27.3", {"start": v(11.75, -26.52) * mm, "end": v(15.44, -34.02) * mm});
            skArc(sketch, "E35.27.4", {"start": v(11.75, -26.52) * mm, "mid": v(10.88, -26.28) * mm, "end": v(10.45, -27.06) * mm});
            skLineSegment(sketch, "E35.27.5", {"start": v(10.45, -27.06) * mm, "end": v(13.14, -34.98) * mm});
            skArc(sketch, "E35.27.6", {"start": v(13.14, -34.98) * mm, "mid": v(13.26, -35.18) * mm, "end": v(13.46, -35.31) * mm});
            skLineSegment(sketch, "E35.27.7", {"start": v(14.41, -35.7) * mm, "end": v(13.46, -35.31) * mm});
            skLineSegment(sketch, "E35.27.8", {"start": v(14.41, -35.7) * mm, "end": v(14.71, -35.83) * mm});
            skLineSegment(sketch, "E35.28.0", {"start": v(19.56, -33.17) * mm, "end": v(19.47, -33.48) * mm});
            skLineSegment(sketch, "E35.28.1", {"start": v(19.56, -33.17) * mm, "end": v(19.82, -32.17) * mm});
            skArc(sketch, "E35.28.2", {"start": v(19.82, -32.17) * mm, "mid": v(19.84, -31.94) * mm, "end": v(19.75, -31.72) * mm});
            skLineSegment(sketch, "E35.28.3", {"start": v(15.1, -24.76) * mm, "end": v(19.75, -31.72) * mm});
            skArc(sketch, "E35.28.4", {"start": v(15.1, -24.76) * mm, "mid": v(14.22, -24.63) * mm, "end": v(13.9, -25.46) * mm});
            skLineSegment(sketch, "E35.28.5", {"start": v(13.9, -25.46) * mm, "end": v(17.6, -32.96) * mm});
            skArc(sketch, "E35.28.6", {"start": v(17.6, -32.96) * mm, "mid": v(17.74, -33.15) * mm, "end": v(17.95, -33.25) * mm});
            skLineSegment(sketch, "E35.28.7", {"start": v(18.95, -33.52) * mm, "end": v(17.95, -33.25) * mm});
            skLineSegment(sketch, "E35.28.8", {"start": v(18.95, -33.52) * mm, "end": v(19.26, -33.6) * mm});
            skLineSegment(sketch, "E35.29.0", {"start": v(23.72, -30.34) * mm, "end": v(23.68, -30.66) * mm});
            skLineSegment(sketch, "E35.29.1", {"start": v(23.72, -30.34) * mm, "end": v(23.85, -29.3) * mm});
            skArc(sketch, "E35.29.2", {"start": v(23.85, -29.3) * mm, "mid": v(23.84, -29.07) * mm, "end": v(23.72, -28.87) * mm});
            skLineSegment(sketch, "E35.29.3", {"start": v(18.21, -22.58) * mm, "end": v(23.72, -28.87) * mm});
            skArc(sketch, "E35.29.4", {"start": v(18.21, -22.58) * mm, "mid": v(17.31, -22.56) * mm, "end": v(17.1, -23.43) * mm});
            skLineSegment(sketch, "E35.29.5", {"start": v(17.1, -23.43) * mm, "end": v(21.75, -30.38) * mm});
            skArc(sketch, "E35.29.6", {"start": v(21.75, -30.38) * mm, "mid": v(21.91, -30.55) * mm, "end": v(22.14, -30.63) * mm});
            skLineSegment(sketch, "E35.29.7", {"start": v(23.16, -30.76) * mm, "end": v(22.14, -30.63) * mm});
            skLineSegment(sketch, "E35.29.8", {"start": v(23.16, -30.76) * mm, "end": v(23.48, -30.8) * mm});
            skLineSegment(sketch, "E35.30.0", {"start": v(27.48, -26.98) * mm, "end": v(27.48, -27.3) * mm});
            skLineSegment(sketch, "E35.30.1", {"start": v(27.48, -26.98) * mm, "end": v(27.48, -25.95) * mm});
            skArc(sketch, "E35.30.2", {"start": v(27.48, -25.95) * mm, "mid": v(27.43, -25.71) * mm, "end": v(27.29, -25.53) * mm});
            skLineSegment(sketch, "E35.30.3", {"start": v(21, -20) * mm, "end": v(27.29, -25.53) * mm});
            skArc(sketch, "E35.30.4", {"start": v(21, -20) * mm, "mid": v(20.11, -20.11) * mm, "end": v(20, -21) * mm});
            skLineSegment(sketch, "E35.30.5", {"start": v(20, -21) * mm, "end": v(25.53, -27.29) * mm});
            skArc(sketch, "E35.30.6", {"start": v(25.53, -27.29) * mm, "mid": v(25.71, -27.43) * mm, "end": v(25.95, -27.48) * mm});
            skLineSegment(sketch, "E35.30.7", {"start": v(26.98, -27.48) * mm, "end": v(25.95, -27.48) * mm});
            skLineSegment(sketch, "E35.30.8", {"start": v(26.98, -27.48) * mm, "end": v(27.3, -27.48) * mm});
            skLineSegment(sketch, "E35.31.0", {"start": v(30.76, -23.16) * mm, "end": v(30.8, -23.48) * mm});
            skLineSegment(sketch, "E35.31.1", {"start": v(30.76, -23.16) * mm, "end": v(30.63, -22.14) * mm});
            skArc(sketch, "E35.31.2", {"start": v(30.63, -22.14) * mm, "mid": v(30.55, -21.91) * mm, "end": v(30.38, -21.75) * mm});
            skLineSegment(sketch, "E35.31.3", {"start": v(23.43, -17.1) * mm, "end": v(30.38, -21.75) * mm});
            skArc(sketch, "E35.31.4", {"start": v(23.43, -17.1) * mm, "mid": v(22.56, -17.31) * mm, "end": v(22.58, -18.21) * mm});
            skLineSegment(sketch, "E35.31.5", {"start": v(22.58, -18.21) * mm, "end": v(28.87, -23.72) * mm});
            skArc(sketch, "E35.31.6", {"start": v(28.87, -23.72) * mm, "mid": v(29.07, -23.84) * mm, "end": v(29.3, -23.85) * mm});
            skLineSegment(sketch, "E35.31.7", {"start": v(30.34, -23.72) * mm, "end": v(29.3, -23.85) * mm});
            skLineSegment(sketch, "E35.31.8", {"start": v(30.34, -23.72) * mm, "end": v(30.66, -23.68) * mm});
            skLineSegment(sketch, "E35.32.0", {"start": v(33.52, -18.95) * mm, "end": v(33.6, -19.26) * mm});
            skLineSegment(sketch, "E35.32.1", {"start": v(33.52, -18.95) * mm, "end": v(33.25, -17.95) * mm});
            skArc(sketch, "E35.32.2", {"start": v(33.25, -17.95) * mm, "mid": v(33.15, -17.74) * mm, "end": v(32.96, -17.6) * mm});
            skLineSegment(sketch, "E35.32.3", {"start": v(25.46, -13.9) * mm, "end": v(32.96, -17.6) * mm});
            skArc(sketch, "E35.32.4", {"start": v(25.46, -13.9) * mm, "mid": v(24.63, -14.22) * mm, "end": v(24.76, -15.1) * mm});
            skLineSegment(sketch, "E35.32.5", {"start": v(24.76, -15.1) * mm, "end": v(31.72, -19.75) * mm});
            skArc(sketch, "E35.32.6", {"start": v(31.72, -19.75) * mm, "mid": v(31.94, -19.84) * mm, "end": v(32.17, -19.82) * mm});
            skLineSegment(sketch, "E35.32.7", {"start": v(33.17, -19.56) * mm, "end": v(32.17, -19.82) * mm});
            skLineSegment(sketch, "E35.32.8", {"start": v(33.17, -19.56) * mm, "end": v(33.48, -19.47) * mm});
            skLineSegment(sketch, "E35.33.0", {"start": v(35.7, -14.41) * mm, "end": v(35.83, -14.71) * mm});
            skLineSegment(sketch, "E35.33.1", {"start": v(35.7, -14.41) * mm, "end": v(35.31, -13.46) * mm});
            skArc(sketch, "E35.33.2", {"start": v(35.31, -13.46) * mm, "mid": v(35.18, -13.26) * mm, "end": v(34.98, -13.14) * mm});
            skLineSegment(sketch, "E35.33.3", {"start": v(27.06, -10.45) * mm, "end": v(34.98, -13.14) * mm});
            skArc(sketch, "E35.33.4", {"start": v(27.06, -10.45) * mm, "mid": v(26.28, -10.88) * mm, "end": v(26.52, -11.75) * mm});
            skLineSegment(sketch, "E35.33.5", {"start": v(26.52, -11.75) * mm, "end": v(34.02, -15.44) * mm});
            skArc(sketch, "E35.33.6", {"start": v(34.02, -15.44) * mm, "mid": v(34.25, -15.5) * mm, "end": v(34.48, -15.46) * mm});
            skLineSegment(sketch, "E35.33.7", {"start": v(35.44, -15.06) * mm, "end": v(34.48, -15.46) * mm});
            skLineSegment(sketch, "E35.33.8", {"start": v(35.44, -15.06) * mm, "end": v(35.74, -14.94) * mm});
            skLineSegment(sketch, "E35.34.0", {"start": v(37.29, -9.63) * mm, "end": v(37.45, -9.9) * mm});
            skLineSegment(sketch, "E35.34.1", {"start": v(37.29, -9.63) * mm, "end": v(36.77, -8.73) * mm});
            skArc(sketch, "E35.34.2", {"start": v(36.77, -8.73) * mm, "mid": v(36.6, -8.56) * mm, "end": v(36.4, -8.46) * mm});
            skLineSegment(sketch, "E35.34.3", {"start": v(28.2, -6.83) * mm, "end": v(36.4, -8.46) * mm});
            skArc(sketch, "E35.34.4", {"start": v(28.2, -6.83) * mm, "mid": v(27.47, -7.36) * mm, "end": v(27.83, -8.18) * mm});
            skLineSegment(sketch, "E35.34.5", {"start": v(27.83, -8.18) * mm, "end": v(35.75, -10.87) * mm});
            skArc(sketch, "E35.34.6", {"start": v(35.75, -10.87) * mm, "mid": v(35.98, -10.9) * mm, "end": v(36.2, -10.82) * mm});
            skLineSegment(sketch, "E35.34.7", {"start": v(37.1, -10.3) * mm, "end": v(36.2, -10.82) * mm});
            skLineSegment(sketch, "E35.34.8", {"start": v(37.1, -10.3) * mm, "end": v(37.38, -10.14) * mm});
            skLineSegment(sketch, "E35.35.0", {"start": v(38.22, -4.68) * mm, "end": v(38.42, -4.93) * mm});
            skLineSegment(sketch, "E35.35.1", {"start": v(38.22, -4.68) * mm, "end": v(37.6, -3.86) * mm});
            skArc(sketch, "E35.35.2", {"start": v(37.6, -3.86) * mm, "mid": v(37.41, -3.7) * mm, "end": v(37.19, -3.64) * mm});
            skLineSegment(sketch, "E35.35.3", {"start": v(28.84, -3.09) * mm, "end": v(37.19, -3.64) * mm});
            skArc(sketch, "E35.35.4", {"start": v(28.84, -3.09) * mm, "mid": v(28.2, -3.71) * mm, "end": v(28.66, -4.48) * mm});
            skLineSegment(sketch, "E35.35.5", {"start": v(28.66, -4.48) * mm, "end": v(36.86, -6.1) * mm});
            skArc(sketch, "E35.35.6", {"start": v(36.86, -6.1) * mm, "mid": v(37.1, -6.1) * mm, "end": v(37.3, -6) * mm});
            skLineSegment(sketch, "E35.35.7", {"start": v(38.13, -5.37) * mm, "end": v(37.3, -6) * mm});
            skLineSegment(sketch, "E35.35.8", {"start": v(38.13, -5.37) * mm, "end": v(38.39, -5.18) * mm});
            skLineSegment(sketch, "E35.36.0", {"start": v(38.5, 0.35) * mm, "end": v(38.73, 0.12) * mm});
            skLineSegment(sketch, "E35.36.1", {"start": v(38.5, 0.35) * mm, "end": v(37.77, 1.08) * mm});
            skArc(sketch, "E35.36.2", {"start": v(37.77, 1.08) * mm, "mid": v(37.58, 1.21) * mm, "end": v(37.34, 1.25) * mm});
            skLineSegment(sketch, "E35.36.3", {"start": v(29, 0.7) * mm, "end": v(37.34, 1.25) * mm});
            skArc(sketch, "E35.36.4", {"start": v(29, 0.7) * mm, "mid": v(28.44, 0) * mm, "end": v(29, -0.7) * mm});
            skLineSegment(sketch, "E35.36.5", {"start": v(29, -0.7) * mm, "end": v(37.34, -1.25) * mm});
            skArc(sketch, "E35.36.6", {"start": v(37.34, -1.25) * mm, "mid": v(37.58, -1.21) * mm, "end": v(37.77, -1.08) * mm});
            skLineSegment(sketch, "E35.36.7", {"start": v(38.5, -0.35) * mm, "end": v(37.77, -1.08) * mm});
            skLineSegment(sketch, "E35.36.8", {"start": v(38.5, -0.35) * mm, "end": v(38.73, -0.12) * mm});
            skLineSegment(sketch, "E35.37.0", {"start": v(38.13, 5.37) * mm, "end": v(38.39, 5.18) * mm});
            skLineSegment(sketch, "E35.37.1", {"start": v(38.13, 5.37) * mm, "end": v(37.3, 6) * mm});
            skArc(sketch, "E35.37.2", {"start": v(37.3, 6) * mm, "mid": v(37.1, 6.1) * mm, "end": v(36.86, 6.1) * mm});
            skLineSegment(sketch, "E35.37.3", {"start": v(28.66, 4.48) * mm, "end": v(36.86, 6.1) * mm});
            skArc(sketch, "E35.37.4", {"start": v(28.66, 4.48) * mm, "mid": v(28.2, 3.71) * mm, "end": v(28.84, 3.09) * mm});
            skLineSegment(sketch, "E35.37.5", {"start": v(28.84, 3.09) * mm, "end": v(37.19, 3.64) * mm});
            skArc(sketch, "E35.37.6", {"start": v(37.19, 3.64) * mm, "mid": v(37.41, 3.7) * mm, "end": v(37.6, 3.86) * mm});
            skLineSegment(sketch, "E35.37.7", {"start": v(38.22, 4.68) * mm, "end": v(37.6, 3.86) * mm});
            skLineSegment(sketch, "E35.37.8", {"start": v(38.22, 4.68) * mm, "end": v(38.42, 4.93) * mm});
            skLineSegment(sketch, "E35.38.0", {"start": v(37.1, 10.3) * mm, "end": v(37.38, 10.14) * mm});
            skLineSegment(sketch, "E35.38.1", {"start": v(37.1, 10.3) * mm, "end": v(36.2, 10.82) * mm});
            skArc(sketch, "E35.38.2", {"start": v(36.2, 10.82) * mm, "mid": v(35.98, 10.9) * mm, "end": v(35.75, 10.87) * mm});
            skLineSegment(sketch, "E35.38.3", {"start": v(27.83, 8.18) * mm, "end": v(35.75, 10.87) * mm});
            skArc(sketch, "E35.38.4", {"start": v(27.83, 8.18) * mm, "mid": v(27.47, 7.36) * mm, "end": v(28.2, 6.83) * mm});
            skLineSegment(sketch, "E35.38.5", {"start": v(28.2, 6.83) * mm, "end": v(36.4, 8.46) * mm});
            skArc(sketch, "E35.38.6", {"start": v(36.4, 8.46) * mm, "mid": v(36.6, 8.56) * mm, "end": v(36.77, 8.73) * mm});
            skLineSegment(sketch, "E35.38.7", {"start": v(37.29, 9.63) * mm, "end": v(36.77, 8.73) * mm});
            skLineSegment(sketch, "E35.38.8", {"start": v(37.29, 9.63) * mm, "end": v(37.45, 9.9) * mm});
            skLineSegment(sketch, "E35.39.0", {"start": v(35.44, 15.06) * mm, "end": v(35.74, 14.94) * mm});
            skLineSegment(sketch, "E35.39.1", {"start": v(35.44, 15.06) * mm, "end": v(34.48, 15.46) * mm});
            skArc(sketch, "E35.39.2", {"start": v(34.48, 15.46) * mm, "mid": v(34.25, 15.5) * mm, "end": v(34.02, 15.44) * mm});
            skLineSegment(sketch, "E35.39.3", {"start": v(26.52, 11.75) * mm, "end": v(34.02, 15.44) * mm});
            skArc(sketch, "E35.39.4", {"start": v(26.52, 11.75) * mm, "mid": v(26.28, 10.88) * mm, "end": v(27.06, 10.45) * mm});
            skLineSegment(sketch, "E35.39.5", {"start": v(27.06, 10.45) * mm, "end": v(34.98, 13.14) * mm});
            skArc(sketch, "E35.39.6", {"start": v(34.98, 13.14) * mm, "mid": v(35.18, 13.26) * mm, "end": v(35.31, 13.46) * mm});
            skLineSegment(sketch, "E35.39.7", {"start": v(35.7, 14.41) * mm, "end": v(35.31, 13.46) * mm});
            skLineSegment(sketch, "E35.39.8", {"start": v(35.7, 14.41) * mm, "end": v(35.83, 14.71) * mm});
            skLineSegment(sketch, "E35.40.0", {"start": v(33.17, 19.56) * mm, "end": v(33.48, 19.47) * mm});
            skLineSegment(sketch, "E35.40.1", {"start": v(33.17, 19.56) * mm, "end": v(32.17, 19.82) * mm});
            skArc(sketch, "E35.40.2", {"start": v(32.17, 19.82) * mm, "mid": v(31.94, 19.84) * mm, "end": v(31.72, 19.75) * mm});
            skLineSegment(sketch, "E35.40.3", {"start": v(24.76, 15.1) * mm, "end": v(31.72, 19.75) * mm});
            skArc(sketch, "E35.40.4", {"start": v(24.76, 15.1) * mm, "mid": v(24.63, 14.22) * mm, "end": v(25.46, 13.9) * mm});
            skLineSegment(sketch, "E35.40.5", {"start": v(25.46, 13.9) * mm, "end": v(32.96, 17.6) * mm});
            skArc(sketch, "E35.40.6", {"start": v(32.96, 17.6) * mm, "mid": v(33.15, 17.74) * mm, "end": v(33.25, 17.95) * mm});
            skLineSegment(sketch, "E35.40.7", {"start": v(33.52, 18.95) * mm, "end": v(33.25, 17.95) * mm});
            skLineSegment(sketch, "E35.40.8", {"start": v(33.52, 18.95) * mm, "end": v(33.6, 19.26) * mm});
            skLineSegment(sketch, "E35.41.0", {"start": v(30.34, 23.72) * mm, "end": v(30.66, 23.68) * mm});
            skLineSegment(sketch, "E35.41.1", {"start": v(30.34, 23.72) * mm, "end": v(29.3, 23.85) * mm});
            skArc(sketch, "E35.41.2", {"start": v(29.3, 23.85) * mm, "mid": v(29.07, 23.84) * mm, "end": v(28.87, 23.72) * mm});
            skLineSegment(sketch, "E35.41.3", {"start": v(22.58, 18.21) * mm, "end": v(28.87, 23.72) * mm});
            skArc(sketch, "E35.41.4", {"start": v(22.58, 18.21) * mm, "mid": v(22.56, 17.31) * mm, "end": v(23.43, 17.1) * mm});
            skLineSegment(sketch, "E35.41.5", {"start": v(23.43, 17.1) * mm, "end": v(30.38, 21.75) * mm});
            skArc(sketch, "E35.41.6", {"start": v(30.38, 21.75) * mm, "mid": v(30.55, 21.91) * mm, "end": v(30.63, 22.14) * mm});
            skLineSegment(sketch, "E35.41.7", {"start": v(30.76, 23.16) * mm, "end": v(30.63, 22.14) * mm});
            skLineSegment(sketch, "E35.41.8", {"start": v(30.76, 23.16) * mm, "end": v(30.8, 23.48) * mm});
            skLineSegment(sketch, "E35.42.0", {"start": v(26.98, 27.48) * mm, "end": v(27.3, 27.48) * mm});
            skLineSegment(sketch, "E35.42.1", {"start": v(26.98, 27.48) * mm, "end": v(25.95, 27.48) * mm});
            skArc(sketch, "E35.42.2", {"start": v(25.95, 27.48) * mm, "mid": v(25.71, 27.43) * mm, "end": v(25.53, 27.29) * mm});
            skLineSegment(sketch, "E35.42.3", {"start": v(20, 21) * mm, "end": v(25.53, 27.29) * mm});
            skArc(sketch, "E35.42.4", {"start": v(20, 21) * mm, "mid": v(20.11, 20.11) * mm, "end": v(21, 20) * mm});
            skLineSegment(sketch, "E35.42.5", {"start": v(21, 20) * mm, "end": v(27.29, 25.53) * mm});
            skArc(sketch, "E35.42.6", {"start": v(27.29, 25.53) * mm, "mid": v(27.43, 25.71) * mm, "end": v(27.48, 25.95) * mm});
            skLineSegment(sketch, "E35.42.7", {"start": v(27.48, 26.98) * mm, "end": v(27.48, 25.95) * mm});
            skLineSegment(sketch, "E35.42.8", {"start": v(27.48, 26.98) * mm, "end": v(27.48, 27.3) * mm});
            skLineSegment(sketch, "E35.43.0", {"start": v(23.16, 30.76) * mm, "end": v(23.48, 30.8) * mm});
            skLineSegment(sketch, "E35.43.1", {"start": v(23.16, 30.76) * mm, "end": v(22.14, 30.63) * mm});
            skArc(sketch, "E35.43.2", {"start": v(22.14, 30.63) * mm, "mid": v(21.91, 30.55) * mm, "end": v(21.75, 30.38) * mm});
            skLineSegment(sketch, "E35.43.3", {"start": v(17.1, 23.43) * mm, "end": v(21.75, 30.38) * mm});
            skArc(sketch, "E35.43.4", {"start": v(17.1, 23.43) * mm, "mid": v(17.31, 22.56) * mm, "end": v(18.21, 22.58) * mm});
            skLineSegment(sketch, "E35.43.5", {"start": v(18.21, 22.58) * mm, "end": v(23.72, 28.87) * mm});
            skArc(sketch, "E35.43.6", {"start": v(23.72, 28.87) * mm, "mid": v(23.84, 29.07) * mm, "end": v(23.85, 29.3) * mm});
            skLineSegment(sketch, "E35.43.7", {"start": v(23.72, 30.34) * mm, "end": v(23.85, 29.3) * mm});
            skLineSegment(sketch, "E35.43.8", {"start": v(23.72, 30.34) * mm, "end": v(23.68, 30.66) * mm});
            skLineSegment(sketch, "E35.44.0", {"start": v(18.95, 33.52) * mm, "end": v(19.26, 33.6) * mm});
            skLineSegment(sketch, "E35.44.1", {"start": v(18.95, 33.52) * mm, "end": v(17.95, 33.25) * mm});
            skArc(sketch, "E35.44.2", {"start": v(17.95, 33.25) * mm, "mid": v(17.74, 33.15) * mm, "end": v(17.6, 32.96) * mm});
            skLineSegment(sketch, "E35.44.3", {"start": v(13.9, 25.46) * mm, "end": v(17.6, 32.96) * mm});
            skArc(sketch, "E35.44.4", {"start": v(13.9, 25.46) * mm, "mid": v(14.22, 24.63) * mm, "end": v(15.1, 24.76) * mm});
            skLineSegment(sketch, "E35.44.5", {"start": v(15.1, 24.76) * mm, "end": v(19.75, 31.72) * mm});
            skArc(sketch, "E35.44.6", {"start": v(19.75, 31.72) * mm, "mid": v(19.84, 31.94) * mm, "end": v(19.82, 32.17) * mm});
            skLineSegment(sketch, "E35.44.7", {"start": v(19.56, 33.17) * mm, "end": v(19.82, 32.17) * mm});
            skLineSegment(sketch, "E35.44.8", {"start": v(19.56, 33.17) * mm, "end": v(19.47, 33.48) * mm});
            skLineSegment(sketch, "E35.45.0", {"start": v(14.41, 35.7) * mm, "end": v(14.71, 35.83) * mm});
            skLineSegment(sketch, "E35.45.1", {"start": v(14.41, 35.7) * mm, "end": v(13.46, 35.31) * mm});
            skArc(sketch, "E35.45.2", {"start": v(13.46, 35.31) * mm, "mid": v(13.26, 35.18) * mm, "end": v(13.14, 34.98) * mm});
            skLineSegment(sketch, "E35.45.3", {"start": v(10.45, 27.06) * mm, "end": v(13.14, 34.98) * mm});
            skArc(sketch, "E35.45.4", {"start": v(10.45, 27.06) * mm, "mid": v(10.88, 26.28) * mm, "end": v(11.75, 26.52) * mm});
            skLineSegment(sketch, "E35.45.5", {"start": v(11.75, 26.52) * mm, "end": v(15.44, 34.02) * mm});
            skArc(sketch, "E35.45.6", {"start": v(15.44, 34.02) * mm, "mid": v(15.5, 34.25) * mm, "end": v(15.46, 34.48) * mm});
            skLineSegment(sketch, "E35.45.7", {"start": v(15.06, 35.44) * mm, "end": v(15.46, 34.48) * mm});
            skLineSegment(sketch, "E35.45.8", {"start": v(15.06, 35.44) * mm, "end": v(14.94, 35.74) * mm});
            skLineSegment(sketch, "E35.46.0", {"start": v(9.63, 37.29) * mm, "end": v(9.9, 37.45) * mm});
            skLineSegment(sketch, "E35.46.1", {"start": v(9.63, 37.29) * mm, "end": v(8.73, 36.77) * mm});
            skArc(sketch, "E35.46.2", {"start": v(8.73, 36.77) * mm, "mid": v(8.56, 36.6) * mm, "end": v(8.46, 36.4) * mm});
            skLineSegment(sketch, "E35.46.3", {"start": v(6.83, 28.2) * mm, "end": v(8.46, 36.4) * mm});
            skArc(sketch, "E35.46.4", {"start": v(6.83, 28.2) * mm, "mid": v(7.36, 27.47) * mm, "end": v(8.18, 27.83) * mm});
            skLineSegment(sketch, "E35.46.5", {"start": v(8.18, 27.83) * mm, "end": v(10.87, 35.75) * mm});
            skArc(sketch, "E35.46.6", {"start": v(10.87, 35.75) * mm, "mid": v(10.9, 35.98) * mm, "end": v(10.82, 36.2) * mm});
            skLineSegment(sketch, "E35.46.7", {"start": v(10.3, 37.1) * mm, "end": v(10.82, 36.2) * mm});
            skLineSegment(sketch, "E35.46.8", {"start": v(10.3, 37.1) * mm, "end": v(10.14, 37.38) * mm});
            skLineSegment(sketch, "E35.47.0", {"start": v(4.68, 38.22) * mm, "end": v(4.93, 38.42) * mm});
            skLineSegment(sketch, "E35.47.1", {"start": v(4.68, 38.22) * mm, "end": v(3.86, 37.6) * mm});
            skArc(sketch, "E35.47.2", {"start": v(3.86, 37.6) * mm, "mid": v(3.7, 37.41) * mm, "end": v(3.64, 37.19) * mm});
            skLineSegment(sketch, "E35.47.3", {"start": v(3.09, 28.84) * mm, "end": v(3.64, 37.19) * mm});
            skArc(sketch, "E35.47.4", {"start": v(3.09, 28.84) * mm, "mid": v(3.71, 28.2) * mm, "end": v(4.48, 28.66) * mm});
            skLineSegment(sketch, "E35.47.5", {"start": v(4.48, 28.66) * mm, "end": v(6.1, 36.86) * mm});
            skArc(sketch, "E35.47.6", {"start": v(6.1, 36.86) * mm, "mid": v(6.1, 37.1) * mm, "end": v(6, 37.3) * mm});
            skLineSegment(sketch, "E35.47.7", {"start": v(5.37, 38.13) * mm, "end": v(6, 37.3) * mm});
            skLineSegment(sketch, "E35.47.8", {"start": v(5.37, 38.13) * mm, "end": v(5.18, 38.39) * mm});
            skArc(sketch, "E36.trimOffspring", {"start": v(4.93, 38.42) * mm, "mid": v(2.53, 38.65) * mm, "end": v(0.12, 38.73) * mm});
            skArc(sketch, "E37.trimOffspring", {"start": v(14.71, 35.83) * mm, "mid": v(12.45, 36.68) * mm, "end": v(10.14, 37.38) * mm});
            skArc(sketch, "E38.trimOffspring", {"start": v(9.9, 37.45) * mm, "mid": v(7.56, 38) * mm, "end": v(5.18, 38.39) * mm});
            skArc(sketch, "E39.trimOffspring", {"start": v(19.26, 33.6) * mm, "mid": v(17.13, 34.74) * mm, "end": v(14.94, 35.74) * mm});
            skArc(sketch, "E40.trimOffspring", {"start": v(23.48, 30.8) * mm, "mid": v(21.52, 32.2) * mm, "end": v(19.47, 33.48) * mm});
            skArc(sketch, "E41.trimOffspring", {"start": v(27.3, 27.48) * mm, "mid": v(25.54, 29.12) * mm, "end": v(23.68, 30.66) * mm});
            skArc(sketch, "E42.trimOffspring", {"start": v(30.66, 23.68) * mm, "mid": v(29.12, 25.54) * mm, "end": v(27.48, 27.3) * mm});
            skArc(sketch, "E43.trimOffspring", {"start": v(33.48, 19.47) * mm, "mid": v(32.2, 21.52) * mm, "end": v(30.8, 23.48) * mm});
            skArc(sketch, "E44.trimOffspring", {"start": v(35.74, 14.94) * mm, "mid": v(34.74, 17.13) * mm, "end": v(33.6, 19.26) * mm});
            skArc(sketch, "E45.trimOffspring", {"start": v(37.38, 10.14) * mm, "mid": v(36.68, 12.45) * mm, "end": v(35.83, 14.71) * mm});
            skArc(sketch, "E46.trimOffspring", {"start": v(38.39, 5.18) * mm, "mid": v(38, 7.56) * mm, "end": v(37.45, 9.9) * mm});
            skArc(sketch, "E47.trimOffspring", {"start": v(38.73, 0.12) * mm, "mid": v(38.65, 2.53) * mm, "end": v(38.42, 4.93) * mm});
            skArc(sketch, "E48.trimOffspring", {"start": v(38.42, -4.93) * mm, "mid": v(38.65, -2.53) * mm, "end": v(38.73, -0.12) * mm});
            skArc(sketch, "E49.trimOffspring", {"start": v(37.45, -9.9) * mm, "mid": v(38, -7.56) * mm, "end": v(38.39, -5.18) * mm});
            skArc(sketch, "E50.trimOffspring", {"start": v(35.83, -14.71) * mm, "mid": v(36.68, -12.45) * mm, "end": v(37.38, -10.14) * mm});
            skArc(sketch, "E51.trimOffspring", {"start": v(33.6, -19.26) * mm, "mid": v(34.74, -17.13) * mm, "end": v(35.74, -14.94) * mm});
            skArc(sketch, "E52.trimOffspring", {"start": v(30.8, -23.48) * mm, "mid": v(32.2, -21.52) * mm, "end": v(33.48, -19.47) * mm});
            skArc(sketch, "E53.trimOffspring", {"start": v(27.48, -27.3) * mm, "mid": v(29.12, -25.54) * mm, "end": v(30.66, -23.68) * mm});
            skArc(sketch, "E54.trimOffspring", {"start": v(23.68, -30.66) * mm, "mid": v(25.54, -29.12) * mm, "end": v(27.3, -27.48) * mm});
            skArc(sketch, "E55.trimOffspring", {"start": v(19.47, -33.48) * mm, "mid": v(21.52, -32.2) * mm, "end": v(23.48, -30.8) * mm});
            skArc(sketch, "E56.trimOffspring", {"start": v(14.94, -35.74) * mm, "mid": v(17.13, -34.74) * mm, "end": v(19.26, -33.6) * mm});
            skArc(sketch, "E57.trimOffspring", {"start": v(10.14, -37.38) * mm, "mid": v(12.45, -36.68) * mm, "end": v(14.71, -35.83) * mm});
            skArc(sketch, "E58.trimOffspring", {"start": v(0.12, -38.73) * mm, "mid": v(2.53, -38.65) * mm, "end": v(4.93, -38.42) * mm});
            skArc(sketch, "E59.trimOffspring", {"start": v(5.18, -38.39) * mm, "mid": v(7.56, -38) * mm, "end": v(9.9, -37.45) * mm});
            skArc(sketch, "E60.trimOffspring", {"start": v(-4.93, -38.42) * mm, "mid": v(-2.53, -38.65) * mm, "end": v(-0.12, -38.73) * mm});
            skArc(sketch, "E61.trimOffspring", {"start": v(-9.9, -37.45) * mm, "mid": v(-7.56, -38) * mm, "end": v(-5.18, -38.39) * mm});
            skArc(sketch, "E62.trimOffspring", {"start": v(-14.71, -35.83) * mm, "mid": v(-12.45, -36.68) * mm, "end": v(-10.14, -37.38) * mm});
            skArc(sketch, "E63.trimOffspring", {"start": v(-19.26, -33.6) * mm, "mid": v(-17.13, -34.74) * mm, "end": v(-14.94, -35.74) * mm});
            skArc(sketch, "E64.trimOffspring", {"start": v(-23.48, -30.8) * mm, "mid": v(-21.52, -32.2) * mm, "end": v(-19.47, -33.48) * mm});
            skArc(sketch, "E65.trimOffspring", {"start": v(-27.3, -27.48) * mm, "mid": v(-25.54, -29.12) * mm, "end": v(-23.68, -30.66) * mm});
            skArc(sketch, "E66.trimOffspring", {"start": v(-30.66, -23.68) * mm, "mid": v(-29.12, -25.54) * mm, "end": v(-27.48, -27.3) * mm});
            skArc(sketch, "E67.trimOffspring", {"start": v(-33.48, -19.47) * mm, "mid": v(-32.2, -21.52) * mm, "end": v(-30.8, -23.48) * mm});
            skArc(sketch, "E68.trimOffspring", {"start": v(-35.74, -14.94) * mm, "mid": v(-34.74, -17.13) * mm, "end": v(-33.6, -19.26) * mm});
            skArc(sketch, "E69.trimOffspring", {"start": v(-37.38, -10.14) * mm, "mid": v(-36.68, -12.45) * mm, "end": v(-35.83, -14.71) * mm});
            skArc(sketch, "E70.trimOffspring", {"start": v(-38.39, -5.18) * mm, "mid": v(-38, -7.56) * mm, "end": v(-37.45, -9.9) * mm});
            skArc(sketch, "E71.trimOffspring", {"start": v(-38.73, -0.12) * mm, "mid": v(-38.65, -2.53) * mm, "end": v(-38.42, -4.93) * mm});
            skArc(sketch, "E72.trimOffspring", {"start": v(-38.42, 4.93) * mm, "mid": v(-38.65, 2.53) * mm, "end": v(-38.73, 0.12) * mm});
            skArc(sketch, "E73.trimOffspring", {"start": v(-37.45, 9.9) * mm, "mid": v(-38, 7.56) * mm, "end": v(-38.39, 5.18) * mm});
            skArc(sketch, "E74.trimOffspring", {"start": v(-35.83, 14.71) * mm, "mid": v(-36.68, 12.45) * mm, "end": v(-37.38, 10.14) * mm});
            skArc(sketch, "E75.trimOffspring", {"start": v(-33.6, 19.26) * mm, "mid": v(-34.74, 17.13) * mm, "end": v(-35.74, 14.94) * mm});
            skArc(sketch, "E76.trimOffspring", {"start": v(-30.8, 23.48) * mm, "mid": v(-32.2, 21.52) * mm, "end": v(-33.48, 19.47) * mm});
            skArc(sketch, "E77.trimOffspring", {"start": v(-27.48, 27.3) * mm, "mid": v(-29.12, 25.54) * mm, "end": v(-30.66, 23.68) * mm});
            skArc(sketch, "E78.trimOffspring", {"start": v(-23.68, 30.66) * mm, "mid": v(-25.54, 29.12) * mm, "end": v(-27.3, 27.48) * mm});
            skArc(sketch, "E79.trimOffspring", {"start": v(-19.47, 33.48) * mm, "mid": v(-21.52, 32.2) * mm, "end": v(-23.48, 30.8) * mm});
            skArc(sketch, "E80.trimOffspring", {"start": v(-14.94, 35.74) * mm, "mid": v(-17.13, 34.74) * mm, "end": v(-19.26, 33.6) * mm});
            skArc(sketch, "E81.trimOffspring", {"start": v(-10.14, 37.38) * mm, "mid": v(-12.45, 36.68) * mm, "end": v(-14.71, 35.83) * mm});
            skArc(sketch, "E82.trimOffspring", {"start": v(-5.18, 38.39) * mm, "mid": v(-7.56, 38) * mm, "end": v(-9.9, 37.45) * mm});
            skSolve(sketch);
        }
        {
            var Q0;
            Q0=makeQuery(id+"F0.imprint","IMPRINT",FACE,{"disambiguationData":[TD([[makeQuery(id+"F0.imprint","IMPRINT",EDGE,{"derivedFrom":sQuery(id+"F0.wireOp",EDGE,"E0")}),-1.0]])]});
            extrude(context, id + "F1", {"entities" : qUnion([Q0]), "depth" : 0.5 * mm});
        }
    });
